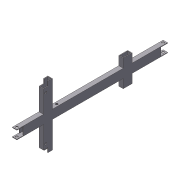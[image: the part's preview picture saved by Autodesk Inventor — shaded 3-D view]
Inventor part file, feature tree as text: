
AUTODESK INVENTOR PART (.ipt)
format: ipt  version: 2012 (Build 160160000, 160)  size: 196,608 bytes
history: native  units: in
note: dims shown in document units (in); Inventor stores cm internally (conversion verified against a paired STEP export)
features: extrude x9, sketch x9, shell x1
ambient origin geometry x8: Origin, YZ Plane, XZ Plane, XY Plane, X Axis, Y Axis, Z Axis, Center Point
bodies: Solid1 (feature_tree)
feature tree (19):
  extrude  "Extrusion1"  Depth=2.0in
  extrude  "Extrusion2"  Depth=2.0in
  extrude  "Extrusion4"  Depth=2.0in TaperAngle=0.0deg
  shell  "Shell3"  Thickness=2.0in
  extrude  "Extrusion5"  Depth=4.0in TaperAngle=0.0deg
  extrude  "Extrusion6"  Depth=0.125in
  extrude  "Extrusion7"  Depth=0.125in
  extrude  "Extrusion8"  TaperAngle=0.0deg  [1 undecoded]
  extrude  "Extrusion9"  Depth=0.5in
  extrude  "Extrusion10"  Depth=2.0in TaperAngle=0.0deg
  sketch  "Sketch1"  dims[d0=1.0in d1=2.0in]
  sketch  "Sketch2"  dims[d2=34.0in d3=0.0in d5=2.0in]
  sketch  "Sketch4"  dims[d6=24.0in d7=2.0in d8=0.0in d14=2.0in]
  sketch  "Sketch5"  dims[d15=6.0in d16=4.0in d17=0.0in]
  sketch  "Sketch6"  dims[d18=6.0in d19=8.0in d20=0.0in d21=0.0in d22=0.125in]
  sketch  "Sketch7"  dims[d23=1.75in d24=0.125in]
  sketch  "Sketch8"  dims[d25=1.5in d26=0.0in d27=0.0in]
  sketch  "Sketch9"  dims[d28=0.5in d29=0.5in]
  sketch  "Sketch10"  dims[d30=0.5in d31=2.0in d32=0.0in d33=0.5in d34=0.5in d35=0.5in d36=2.0in d37=0.0in d38=1.0in d39=1.0in d40=2.0in d41=0.0in d42=0.5in d43=1.0in d44=0.5in d45=1.0in d46=0.5in d47=2.0in d48=0.0in d49=0.5in d50=0.5in d51=1.5in d52=2.0in d53=0.0in]
note: 1 required parameter value undecoded (feature->parameter linkage not recoverable at this tier; creation-order binding heuristic only, values carry confidence <= 0.55)
